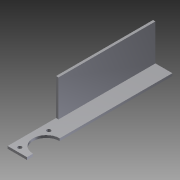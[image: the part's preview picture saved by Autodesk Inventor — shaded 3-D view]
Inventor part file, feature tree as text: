
AUTODESK INVENTOR PART (.ipt)
format: ipt  version: 2012 (Build 160160000, 160)  size: 86,016 bytes
history: native  units: in
note: dims shown in document units (in); Inventor stores cm internally (conversion verified against a paired STEP export)
features: other x3, sketch x2
ambient origin geometry x8: Origin, YZ Plane, XZ Plane, XY Plane, X Axis, Y Axis, Z Axis, Center Point
bodies: Solid1 (feature_tree)
feature tree (5):
  other  "8 ball corner L.ipt"
  other  "Solid1::8 ball corner L.ipt"
  sketch  "Sketch1"  dims[d0=0.3937in]
  sketch  "Sketch2"
  other  "TaggingFeature1"
